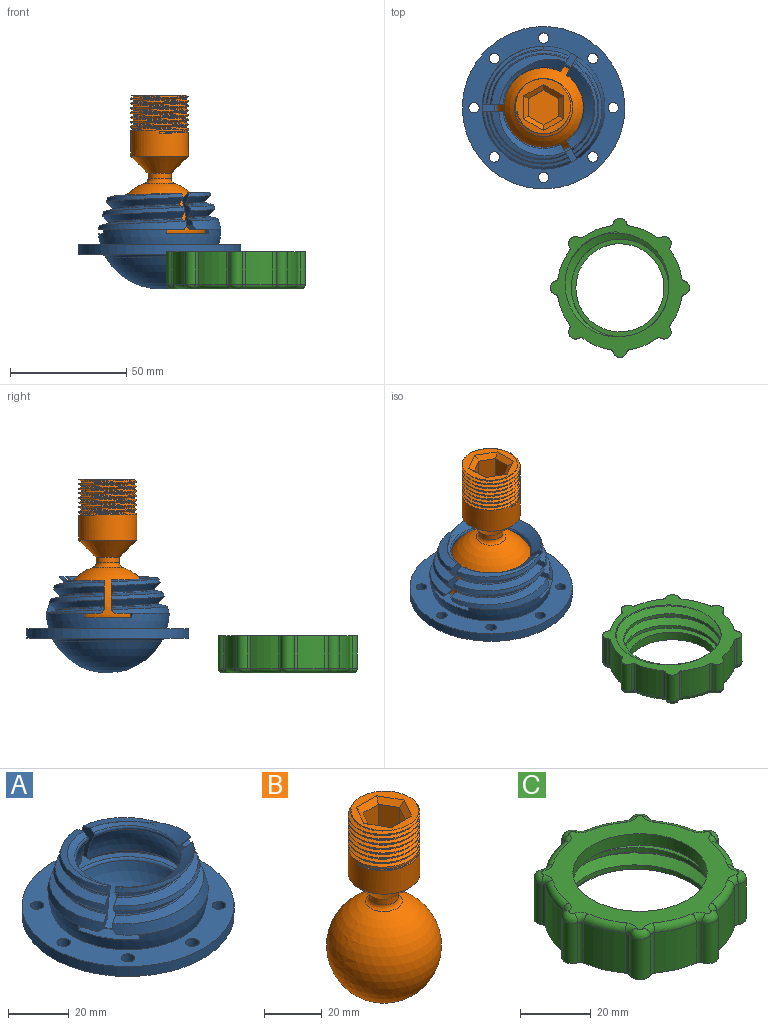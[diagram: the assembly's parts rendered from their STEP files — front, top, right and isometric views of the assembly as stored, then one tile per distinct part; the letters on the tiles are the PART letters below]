
ASSEMBLY  parts=3 mates=3
PART A: 87 faces, bbox 70.1x70.1x42.7 mm
  f0: sphere r=26.5mm, area 986.5mm2, adj f4,f7,f10,f43,f55,f62,f72,f73
  f1: torus R=23.66mm, axis (0,0,1), area 96.9mm2, adj f39,f62,f74,f77
  f2: torus R=23.66mm, axis (0,0,1), area 96.9mm2, adj f38,f62,f72,f75
  f3: torus R=23.66mm, axis (0,0,1), area 96.9mm2, adj f37,f62,f73,f76
  f4: cone r=26.49mm half-angle=16.6deg, axis (0,0,-1), area 136.5mm2, adj f0,f17,f37,f58,f61,f67,f71,f80
  f5: cone r=26.49mm half-angle=16.6deg, axis (0,0,-1), area 79.6mm2, adj f18,f31,f67,f71
  f6: cone r=26.49mm half-angle=16.6deg, axis (0,0,-1), area 0.2mm2, adj f15,f32,f71
  f7: cone r=26.49mm half-angle=16.6deg, axis (0,0,-1), area 237.4mm2, adj f0,f19,f38,f68,f70,f81,f82
  f8: cone r=26.49mm half-angle=16.6deg, axis (0,0,-1), area 81.7mm2, adj f20,f33,f68,f70
  f9: cone r=26.49mm half-angle=16.6deg, axis (0,0,-1), area 51mm2, adj f16,f21,f34,f68,f70
  f10: cone r=26.49mm half-angle=16.6deg, axis (0,0,-1), area 132.4mm2, adj f0,f22,f39,f66,f69,f78,f83
  f11: cone r=26.49mm half-angle=16.6deg, axis (0,0,-1), area 84mm2, adj f23,f35,f66,f69
  f12: cone r=26.49mm half-angle=16.6deg, axis (0,0,-1), area 77.4mm2, adj f24,f36,f66,f69
  f13: sphere r=20.5mm, area 427.2mm2, adj f40,f67,f71,f79,f80,f84
  f14: sphere r=20.5mm, area 427.2mm2, adj f41,f68,f70,f81,f82,f85
  f15: cone r=16.79mm half-angle=55deg, axis (0,0,1), area 94.5mm2, adj f6,f18,f26,f32,f67,f71,f84
  f16: cone r=16.79mm half-angle=55deg, axis (0,0,1), area 189mm2, adj f9,f21,f68,f70,f85
  f17: bspline ~35.31x23.42mm, area 168.3mm2, adj f4,f25,f67,f71
  f18: bspline ~32.62x21.64mm, area 153mm2, adj f5,f15,f26,f67,f71
  f19: bspline ~41.97x13.46mm, area 173mm2, adj f7,f27,f68,f70
  f20: bspline ~38.86x12.57mm, area 158.8mm2, adj f8,f28,f68,f70
  f21: bspline ~11.92x11.48mm, area 2.8mm2, adj f9,f16,f68
  f22: bspline ~46.19x35.35mm, area 177.7mm2, adj f10,f29,f66,f69
  f23: bspline ~34.69x22.53mm, area 163.6mm2, adj f11,f30,f66,f69
  f24: bspline ~32x20.72mm, area 81.2mm2, adj f12,f57,f66,f69
  f25: bspline ~36.61x29.95mm, area 31.9mm2, adj f17,f31,f67,f71
  f26: bspline ~31.94x21.48mm, area 19.4mm2, adj f15,f18,f32,f71
  f27: bspline ~42.83x19.09mm, area 32.9mm2, adj f19,f33,f68,f70
  f28: bspline ~37.07x14.32mm, area 29.9mm2, adj f20,f34,f68,f70
  f29: bspline ~39.61x30.32mm, area 33.9mm2, adj f22,f35,f66,f69
  f30: bspline ~37.57x25.78mm, area 30.9mm2, adj f23,f36,f66,f69
  f31: bspline ~40.77x33.36mm, area 162.5mm2, adj f5,f25,f67,f71
  f32: bspline ~20.18x5.19mm, area 41.2mm2, adj f6,f15,f26,f71
  f33: bspline ~39.74x12.21mm, area 167.3mm2, adj f8,f27,f68,f70
  f34: bspline ~36.63x11.33mm, area 153.1mm2, adj f9,f28,f68,f70
  f35: bspline ~43.88x33.58mm, area 172mm2, adj f11,f29,f66,f69
  f36: bspline ~41.98x28.79mm, area 157.8mm2, adj f12,f30,f66,f69
  f37: plane 36.88x23.3mm, normal (0,0,-1), area 130mm2, adj f3,f4,f40,f55,f73,f76,f79,f80
  f38: plane 42.58x10.41mm, normal (0,0,-1), area 130mm2, adj f2,f7,f41,f72,f75,f81,f82
  f39: plane 36.88x23.3mm, normal (0,0,-1), area 130mm2, adj f1,f10,f64,f74,f77,f78,f83
  f40: torus R=21.5mm, axis (0,0,1), area 60mm2, adj f13,f37,f79,f80
  f41: torus R=21.5mm, axis (0,0,1), area 60mm2, adj f14,f38,f81,f82
  f42: cylinder r=35mm len=70mm, axis (0,0,-1), area 879.6mm2, adj f43,f44
  f43: plane 70x70mm, normal (0,0,1), area 1691.7mm2, adj f0,f42,f45,f46,f47,f48,f49,f50
  f44: plane 70x70mm, normal (0,0,-1), area 1694.9mm2, adj f42,f45,f46,f47,f48,f49,f50,f51
  f45: cylinder r=2.25mm len=4.5mm, axis (0,0,1), area 56.5mm2, adj f43,f44
  f46: cylinder r=2.25mm len=4.5mm, axis (0,0,1), area 56.5mm2, adj f43,f44
  f47: cylinder r=2.25mm len=4.5mm, axis (0,0,1), area 56.5mm2, adj f43,f44
  f48: cylinder r=2.25mm len=4.5mm, axis (0,0,1), area 56.5mm2, adj f43,f44
  f49: cylinder r=2.25mm len=4.5mm, axis (0,0,1), area 56.5mm2, adj f43,f44
  f50: cylinder r=2.25mm len=4.5mm, axis (0,0,1), area 56.5mm2, adj f43,f44
  f51: cylinder r=2.25mm len=4.5mm, axis (0,0,1), area 56.5mm2, adj f43,f44
  f52: cylinder r=2.25mm len=4.5mm, axis (0,0,1), area 56.5mm2, adj f43,f44
  f53: sphere r=26.5mm, area 2282.3mm2, adj f54
  f54: torus R=25.4mm, axis (0,0,1), area 405.3mm2, adj f44,f53
  f55: cone r=26.49mm half-angle=16.6deg, axis (0,0,-1), area 28.9mm2, adj f0,f37,f59,f79
  f56: sphere r=20.5mm, area 427.2mm2, adj f64,f66,f69,f78,f83,f86
  f57: cone r=16.79mm half-angle=55deg, axis (0,0,1), area 118.9mm2, adj f24,f66,f69,f86
  f58: plane 4.34x3.98mm, normal (0,1,0), area 8.5mm2, adj f4,f59,f60,f61
  f59: bspline ~26.01x25.19mm, area 139.2mm2, adj f55,f58,f60,f67,f79
  f60: bspline ~30.28x22.55mm, area 26.7mm2, adj f58,f59,f61,f67
  f61: bspline ~24.72x23.86mm, area 134.9mm2, adj f4,f58,f60,f67
  f62: plane 52.34x50.01mm, normal (0,0,1), area 516.6mm2, adj f0,f1,f2,f3,f65,f72,f73,f74
  f63: sphere r=20.5mm, area 2173.8mm2, adj f65
  f64: torus R=21.5mm, axis (0,0,1), area 60mm2, adj f39,f56,f78,f83
  f65: torus R=21.16mm, axis (0,0,1), area 180.1mm2, adj f62,f63
  f66: plane 12.97x9.03mm, normal (1,0,0), area 46.7mm2, adj f10,f11,f12,f22,f23,f24,f29,f30
  f67: plane 12.87x8.82mm, normal (-1,0,0), area 46.3mm2, adj f4,f5,f13,f15,f17,f18,f25,f31
  f68: plane 14.34x7.84mm, normal (-0.5,0.87,0), area 50.1mm2, adj f7,f8,f9,f14,f16,f19,f20,f21
  f69: plane 14.24x7.84mm, normal (0.5,-0.87,0), area 50mm2, adj f10,f11,f12,f22,f23,f24,f29,f30
  f70: plane 14.63x7.84mm, normal (0.5,0.87,0), area 50.2mm2, adj f7,f8,f9,f14,f16,f19,f20,f27
  f71: plane 14.63x7.84mm, normal (-0.5,-0.87,0), area 50.2mm2, adj f4,f5,f6,f13,f15,f17,f18,f25
  f72: plane 2.3x2.13mm, normal (0.77,0.64,0), area 4mm2, adj f0,f2,f38,f62
  f73: plane 2.92x2.13mm, normal (-0.17,-0.98,0), area 4mm2, adj f0,f3,f37,f62
  f74: plane 2.92x2.13mm, normal (0.17,-0.98,0), area 4mm2, adj f0,f1,f39,f62
  f75: plane 2.3x2.13mm, normal (-0.77,0.64,0), area 4mm2, adj f0,f2,f38,f62
  f76: plane 2.79x2.13mm, normal (-0.94,0.34,0), area 4mm2, adj f0,f3,f37,f62
  f77: plane 2.79x2.13mm, normal (0.94,0.34,0), area 4mm2, adj f0,f1,f39,f62
  f78: plane 5.93x1.51mm, normal (0.71,0,-0.71), area 12mm2, adj f10,f39,f56,f64,f66
  f79: plane 5.93x1.51mm, normal (-0.71,0,-0.71), area 12mm2, adj f13,f37,f40,f55,f59,f67
  f80: plane 5.85x3.79mm, normal (-0.35,-0.61,-0.71), area 12mm2, adj f4,f13,f37,f40,f71
  f81: plane 5.29x4.25mm, normal (0.35,0.61,-0.71), area 12mm2, adj f7,f14,f38,f41,f70
  f82: plane 5.29x4.25mm, normal (-0.35,0.61,-0.71), area 12mm2, adj f7,f14,f38,f41,f68
  f83: plane 5.85x3.79mm, normal (0.35,-0.61,-0.71), area 12mm2, adj f10,f39,f56,f64,f69
  f84: torus R=18.17mm, axis (0,0,-1), area 50.6mm2, adj f13,f15,f67,f71
  f85: torus R=18.17mm, axis (0,0,-1), area 50.6mm2, adj f14,f16,f68,f70
  f86: torus R=18.17mm, axis (0,0,-1), area 50.6mm2, adj f56,f57,f66,f69
PART B: 35 faces, bbox 40.6x40.6x78.4 mm
  f0: plane 24.4x24.3mm, normal (0,0,1), area 187.2mm2, adj f11,f23,f24,f25,f27,f28,f29,f30
  f1: sphere r=20mm, area 4895.9mm2, adj f33
  f2: cylinder r=5mm len=10mm, axis (0,0,-1), area 75.2mm2, adj f12,f33
  f3: cylinder r=12.5mm len=25mm, axis (0,0,-1), area 854.5mm2, adj f4,f12,f20,f21,f22,f25
  f4: cylinder r=12.5mm len=25mm, axis (0,0,-1), area 25.3mm2, adj f3,f5,f21,f24,f25
  f5: cylinder r=12.5mm len=25mm, axis (0,0,-1), area 19.6mm2, adj f4,f6,f24,f25
  f6: cylinder r=12.5mm len=25mm, axis (0,0,-1), area 19.7mm2, adj f5,f7,f24,f25
  f7: cylinder r=12.5mm len=25mm, axis (0,0,-1), area 19.6mm2, adj f6,f8,f24,f25
  f8: cylinder r=12.5mm len=25mm, axis (0,0,-1), area 19.7mm2, adj f7,f9,f24,f25
  f9: cylinder r=12.5mm len=25mm, axis (0,0,-1), area 19.7mm2, adj f8,f10,f24,f25
  f10: cylinder r=12.5mm len=25mm, axis (0,0,-1), area 19.7mm2, adj f9,f11,f24,f25
  f11: cylinder r=12.5mm len=8.76mm, axis (0,0,-1), area 1.2mm2, adj f0,f10,f24
  f12: cone r=8.75mm half-angle=45deg, axis (0,0,1), area 583.1mm2, adj f2,f3
  f13: plane 23x7.62mm, normal (0,-1,0), area 175.3mm2, adj f14,f18,f19,f29
  f14: plane 23x6.6mm, normal (0.87,-0.5,0), area 175.3mm2, adj f13,f15,f19,f31
  f15: plane 23x6.6mm, normal (0.87,0.5,0), area 175.3mm2, adj f14,f16,f19,f32
  f16: plane 23x7.62mm, normal (0,1,0), area 175.3mm2, adj f15,f17,f19,f30
  f17: plane 23x6.6mm, normal (-0.87,0.5,0), area 175.3mm2, adj f16,f18,f19,f28
  f18: plane 23x6.6mm, normal (-0.87,-0.5,0), area 175.3mm2, adj f13,f17,f19,f27
  f19: plane 15.24x13.2mm, normal (0,0,1), area 150.9mm2, adj f13,f14,f15,f16,f17,f18
  f20: plane 0.61x0.2mm, normal (0,-1,0), area 0.1mm2, adj f3,f21,f22,f26
  f21: bspline ~26.6x26.2mm, area 51.3mm2, adj f3,f4,f20,f24,f26
  f22: bspline ~26.6x26.2mm, area 51.3mm2, adj f3,f20,f25,f26
  f23: bspline ~26.37x22.84mm, area 281.1mm2, adj f0,f24,f25,f26
  f24: bspline ~28.87x25mm, area 636.7mm2, adj f0,f4,f5,f6,f7,f8,f9,f10
  f25: bspline ~28.87x25mm, area 684.5mm2, adj f0,f3,f4,f5,f6,f7,f8,f9
  f26: bspline ~24.43x24.02mm, area 41.7mm2, adj f20,f21,f22,f23
  f27: plane 8.6x6.12mm, normal (-0.61,-0.35,0.71), area 24.8mm2, adj f0,f18,f28,f29
  f28: plane 8.6x6.12mm, normal (-0.61,0.35,0.71), area 24.8mm2, adj f0,f17,f27,f30
  f29: plane 9.93x2mm, normal (0,-0.71,0.71), area 24.8mm2, adj f0,f13,f27,f31
  f30: plane 9.93x2mm, normal (0,0.71,0.71), area 24.8mm2, adj f0,f16,f28,f32
  f31: plane 8.6x6.12mm, normal (0.61,-0.35,0.71), area 24.8mm2, adj f0,f14,f29,f32
  f32: plane 8.6x6.12mm, normal (0.61,0.35,0.71), area 24.8mm2, adj f0,f15,f30,f31
  f33: torus R=7mm, axis (0,0,-1), area 85.9mm2, adj f1,f2
  f34: sphere r=14mm, area 2463mm2
PART C: 72 faces, bbox 60.4x60.4x18.8 mm
  f0: cylinder r=27mm len=14mm, axis (0,0,-1), area 181.1mm2, adj f8,f24,f39,f40
  f1: cylinder r=27mm len=14mm, axis (0,0,-1), area 181.1mm2, adj f8,f25,f26,f48
  f2: cylinder r=27mm len=14mm, axis (0,0,-1), area 181.1mm2, adj f8,f27,f36,f56
  f3: cylinder r=27mm len=14mm, axis (0,0,-1), area 181.1mm2, adj f8,f34,f37,f64
  f4: cylinder r=27mm len=14mm, axis (0,0,-1), area 181.1mm2, adj f8,f32,f35,f71
  f5: cylinder r=27mm len=14mm, axis (0,0,-1), area 181.1mm2, adj f8,f28,f33,f63
  f6: cylinder r=27mm len=14mm, axis (0,0,-1), area 181.1mm2, adj f8,f29,f30,f55
  f7: cylinder r=27mm len=14mm, axis (0,0,-1), area 181.1mm2, adj f8,f31,f38,f47
  f8: plane 60.41x60.41mm, normal (0,0,-1), area 823.1mm2, adj f0,f1,f2,f3,f4,f5,f6,f7
  f9: plane 45.15x45.12mm, normal (0,0,-1), area 452.4mm2, adj f10,f12,f13,f14,f15
  f10: cylinder r=19mm len=38mm, axis (0,0,-1), area 477.5mm2, adj f9,f11
  f11: plane 56x56mm, normal (0,0,1), area 899.9mm2, adj f10,f40,f41,f42,f43,f44,f45,f46
  f12: bspline ~56x48.5mm, area 1067mm2, adj f8,f9,f14,f15
  f13: bspline ~56x48.5mm, area 1066.5mm2, adj f8,f9,f14,f15
  f14: bspline ~56.63x49.04mm, area 266.3mm2, adj f8,f9,f12,f13
  f15: cylinder r=21mm len=42mm, axis (0,0,1), area 395.6mm2, adj f8,f9,f12,f13
  f16: cylinder r=3mm len=14mm, axis (0,0,1), area 109.9mm2, adj f8,f38,f39,f43
  f17: cylinder r=3mm len=14mm, axis (0,0,1), area 109.9mm2, adj f8,f30,f31,f51
  f18: cylinder r=3mm len=14mm, axis (0,0,1), area 109.9mm2, adj f8,f28,f29,f59
  f19: cylinder r=3mm len=14mm, axis (0,0,1), area 109.9mm2, adj f8,f32,f33,f67
  f20: cylinder r=3mm len=14mm, axis (0,0,1), area 109.9mm2, adj f8,f34,f35,f68
  f21: cylinder r=3mm len=14mm, axis (0,0,1), area 109.9mm2, adj f8,f36,f37,f60
  f22: cylinder r=3mm len=14mm, axis (0,0,1), area 109.9mm2, adj f8,f26,f27,f52
  f23: cylinder r=3mm len=14mm, axis (0,0,1), area 109.9mm2, adj f8,f24,f25,f44
  f24: cylinder r=1.5mm len=14mm, axis (0,0,-1), area 24.3mm2, adj f0,f8,f23,f42
  f25: cylinder r=1.5mm len=14mm, axis (0,0,-1), area 24.3mm2, adj f1,f8,f23,f46
  f26: cylinder r=1.5mm len=14mm, axis (0,0,-1), area 24.3mm2, adj f1,f8,f22,f50
  f27: cylinder r=1.5mm len=14mm, axis (0,0,-1), area 24.3mm2, adj f2,f8,f22,f54
  f28: cylinder r=1.5mm len=14mm, axis (0,0,-1), area 24.3mm2, adj f5,f8,f18,f61
  f29: cylinder r=1.5mm len=14mm, axis (0,0,-1), area 24.3mm2, adj f6,f8,f18,f57
  f30: cylinder r=1.5mm len=14mm, axis (0,0,-1), area 24.3mm2, adj f6,f8,f17,f53
  f31: cylinder r=1.5mm len=14mm, axis (0,0,-1), area 24.3mm2, adj f7,f8,f17,f49
  f32: cylinder r=1.5mm len=14mm, axis (0,0,-1), area 24.3mm2, adj f4,f8,f19,f69
  f33: cylinder r=1.5mm len=14mm, axis (0,0,-1), area 24.3mm2, adj f5,f8,f19,f65
  f34: cylinder r=1.5mm len=14mm, axis (0,0,-1), area 24.3mm2, adj f3,f8,f20,f66
  f35: cylinder r=1.5mm len=14mm, axis (0,0,-1), area 24.3mm2, adj f4,f8,f20,f70
  f36: cylinder r=1.5mm len=14mm, axis (0,0,-1), area 24.3mm2, adj f2,f8,f21,f58
  f37: cylinder r=1.5mm len=14mm, axis (0,0,-1), area 24.3mm2, adj f3,f8,f21,f62
  f38: cylinder r=1.5mm len=14mm, axis (0,0,-1), area 24.3mm2, adj f7,f8,f16,f45
  f39: cylinder r=1.5mm len=14mm, axis (0,0,-1), area 24.3mm2, adj f0,f8,f16,f41
  f40: torus R=25mm, axis (0,0,1), area 39.6mm2, adj f0,f11,f41,f42
  f41: torus R=3.5mm, axis (0,0,1), area 8.1mm2, adj f11,f39,f40,f43
  f42: torus R=3.5mm, axis (0,0,1), area 8.1mm2, adj f11,f24,f40,f44
  f43: torus R=1mm, axis (0,0,1), area 18.7mm2, adj f11,f16,f41,f45
  f44: torus R=1mm, axis (0,0,1), area 18.7mm2, adj f11,f23,f42,f46
  f45: torus R=3.5mm, axis (0,0,1), area 8.1mm2, adj f11,f38,f43,f47
  f46: torus R=3.5mm, axis (0,0,1), area 8.1mm2, adj f11,f25,f44,f48
  f47: torus R=25mm, axis (0,0,1), area 39.6mm2, adj f7,f11,f45,f49
  f48: torus R=25mm, axis (0,0,1), area 39.6mm2, adj f1,f11,f46,f50
  f49: torus R=3.5mm, axis (0,0,1), area 8.1mm2, adj f11,f31,f47,f51
  f50: torus R=3.5mm, axis (0,0,1), area 8.1mm2, adj f11,f26,f48,f52
  f51: torus R=1mm, axis (0,0,1), area 18.7mm2, adj f11,f17,f49,f53
  f52: torus R=1mm, axis (0,0,1), area 18.7mm2, adj f11,f22,f50,f54
  f53: torus R=3.5mm, axis (0,0,1), area 8.1mm2, adj f11,f30,f51,f55
  f54: torus R=3.5mm, axis (0,0,1), area 8.1mm2, adj f11,f27,f52,f56
  f55: torus R=25mm, axis (0,0,1), area 39.6mm2, adj f6,f11,f53,f57
  f56: torus R=25mm, axis (0,0,1), area 39.6mm2, adj f2,f11,f54,f58
  f57: torus R=3.5mm, axis (0,0,1), area 8.1mm2, adj f11,f29,f55,f59
  f58: torus R=3.5mm, axis (0,0,1), area 8.1mm2, adj f11,f36,f56,f60
  f59: torus R=1mm, axis (0,0,1), area 18.7mm2, adj f11,f18,f57,f61
  f60: torus R=1mm, axis (0,0,1), area 18.7mm2, adj f11,f21,f58,f62
  f61: torus R=3.5mm, axis (0,0,1), area 8.1mm2, adj f11,f28,f59,f63
  f62: torus R=3.5mm, axis (0,0,1), area 8.1mm2, adj f11,f37,f60,f64
  f63: torus R=25mm, axis (0,0,1), area 39.6mm2, adj f5,f11,f61,f65
  f64: torus R=25mm, axis (0,0,1), area 39.6mm2, adj f3,f11,f62,f66
  f65: torus R=3.5mm, axis (0,0,1), area 8.1mm2, adj f11,f33,f63,f67
  f66: torus R=3.5mm, axis (0,0,1), area 8.1mm2, adj f11,f34,f64,f68
  f67: torus R=1mm, axis (0,0,1), area 18.7mm2, adj f11,f19,f65,f69
  f68: torus R=1mm, axis (0,0,1), area 18.7mm2, adj f11,f20,f66,f70
  f69: torus R=3.5mm, axis (0,0,1), area 8.1mm2, adj f11,f32,f67,f71
  f70: torus R=3.5mm, axis (0,0,1), area 8.1mm2, adj f11,f35,f68,f71
  f71: torus R=25mm, axis (0,0,1), area 39.6mm2, adj f4,f11,f69,f70
PLACE A rot(axis=(0,0,1),90deg) t=(16.87,23.85,-4.55)mm fixed
PLACE B rot(axis=(0,0,1),90deg) t=(16.87,23.85,6.95)mm
PLACE C rot(axis=(0,-1,0),180deg) t=(49.77,-53.76,-3.55)mm
MATE parallel A.f50 <-> C.f15  axis (0,0,-1) through (16.87,-6.15,-4.55)mm
MATE ball B.f2 <-> A.f40  axis (0,0,1) through (16.87,23.85,6.95)mm
MATE parallel B.f0 <-> A.f47  axis (0,0,1) through (16.32,25.18,63.95)mm
